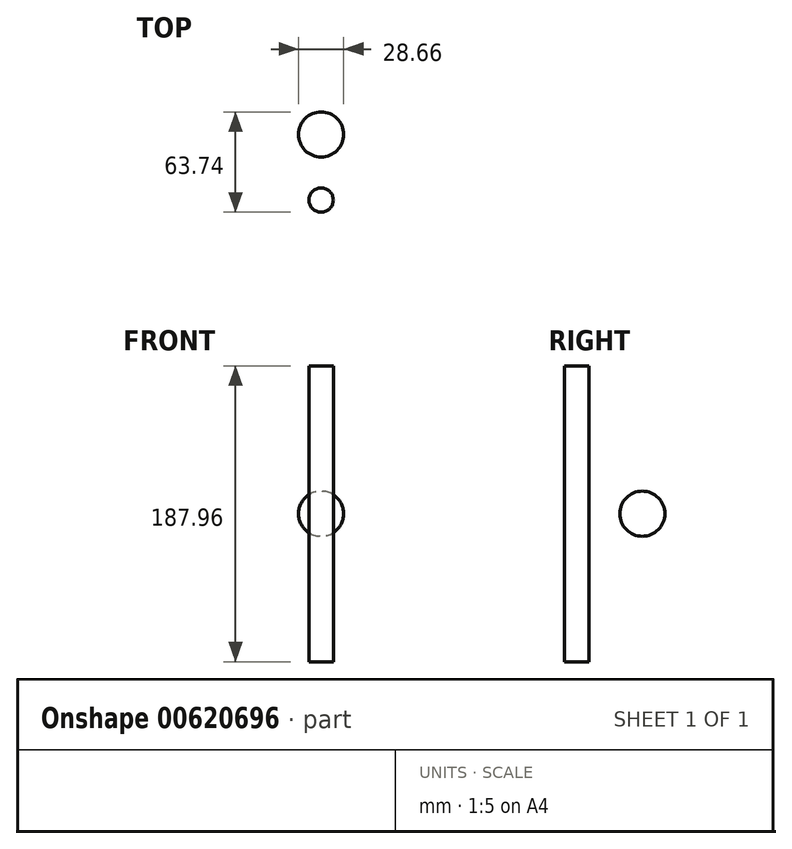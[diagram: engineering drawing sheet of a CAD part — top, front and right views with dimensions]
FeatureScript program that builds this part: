
annotation { "Feature Type Name" : "Feature", "Feature Type Description" : "" }
export const myFeature = defineFeature(function(context is Context, id is Id, definition is map)
    precondition{}
    {
        {
            var Q0;
            Q0=qCreatedBy(makeId("Top.planeOp"),FACE);
            var sketch = newSketch(context, id + "F0", { "sketchPlane" : qUnion([Q0])});
            skCircle(sketch, "E0", {"center": v(0, 0) * mm, "radius": 7.75 * mm});
            skSolve(sketch);
        }
        {
            var Q0;
            Q0=makeQuery(id+"F0.imprint","IMPRINT",FACE,{"disambiguationData":[TD([[makeQuery(id+"F0.imprint","IMPRINT",EDGE,{"derivedFrom":sQuery(id+"F0.wireOp",EDGE,"E0")}),1.0]])]});
            extrude(context, id + "F1", {"entities" : qUnion([Q0]), "depth" : 187.96 * mm, "offsetDistance" : 25.4 * mm, "symmetric" : true});
        }
        {
            var Q0;
            Q0=qCreatedBy(makeId("Top.planeOp"),FACE);
            var sketch = newSketch(context, id + "F2", { "sketchPlane" : qUnion([Q0])});
            skCircle(sketch, "E1", {"center": v(0, 41.66) * mm, "radius": 14.33 * mm});
            skLineSegment(sketch, "E2", {"start": v(0, 41.66) * mm, "end": v(21.82, 41.66) * mm});
            skLineSegment(sketch, "E3", {"start": v(0, 41.66) * mm, "end": v(-28.36, 41.66) * mm});
            skSolve(sketch);
        }
        {
            var Q0;
            {var subQ0=sQuery(id+"F2.wireOp",EDGE,"E2");var subQ1=sQuery(id+"F2.wireOp",EDGE,"E1");var subQ2=makeQuery(id+"F2.imprint","INTERSECT",VERTEX,{"derivedFrom":[subQ1,subQ0]});Q0=makeQuery(id+"F2.imprint","IMPRINT",FACE,{"disambiguationData":[TD([[makeQuery(id+"F2.imprint","IMPRINT",EDGE,{"disambiguationData":[TD([[subQ2,1.0]])],"derivedFrom":subQ1}),1.0]])]});}
            var Q1;
            Q1=sQuery(id+"F2.wireOp",EDGE,"E2");
            revolve(context, id + "F3", {"surfaceOperationType" : NewSurfaceOperationType.NEW, "entities" : qUnion([Q0]), "axis" : qUnion([Q1]), "revolveType" : RevolveType.FULL});
        }
    });
